# Revit family: FU_Modular_Sandler_Bau 8-1
name_source: partatom
category: Furniture
units: mm (PartAtom-declared; Revit-internal decimal feet)

## family parameters
Always vertical = Yes
Cut with Voids When Loaded = No
OmniClass Number = 23.21.23.00
Render Appearance Source = Family Geometry
Room Calculation Point = No
Shared = No
Work Plane-Based = No

## types (2) — shared parameters
Depth = 800 mm  [stored 2.62467 ft]
Height = 420 mm  [stored 1.37795 ft]
Weight Net (Kg) = 15.5
Width = 750 mm  [stored 2.46063 ft]
zero-valued in all types: Default Elevation

## per-type parameters (varying)
| type | Description | Manufacturer | Product Material | Product data url | Product url | URL |
| Bau Pouf Straight | Bau is a modular seating series that ignores conventional ideas of right and wrong. It can be employed as a solitary easy chair or combined to create a playful variety of seating configurations. The collection includes a linking table, whose geometrical edginess contrasts with the sofa’s laid-back personality. | Lammhults | <By Category> | https://bimobject.com | https://www.lammhults.se | https://www.lammhults.se |
| Bau 8.1 | Straight ottoman with shell of fibre board and high resilient polyurethane foam. Adjustable glides. | Sandler | Fabric - Manhattan - Staten YI386 |  |  | https://www.sandlerseating.com |

note: column(s) folded — value = type name in every type: Model

note: [stored X ft] marks values corroborated as IEEE doubles in the binary element streams (Revit-internal decimal feet)

## geometry (parser evidence)
native form markers: Sweep x2
no freeform markers — native parametric forms only
